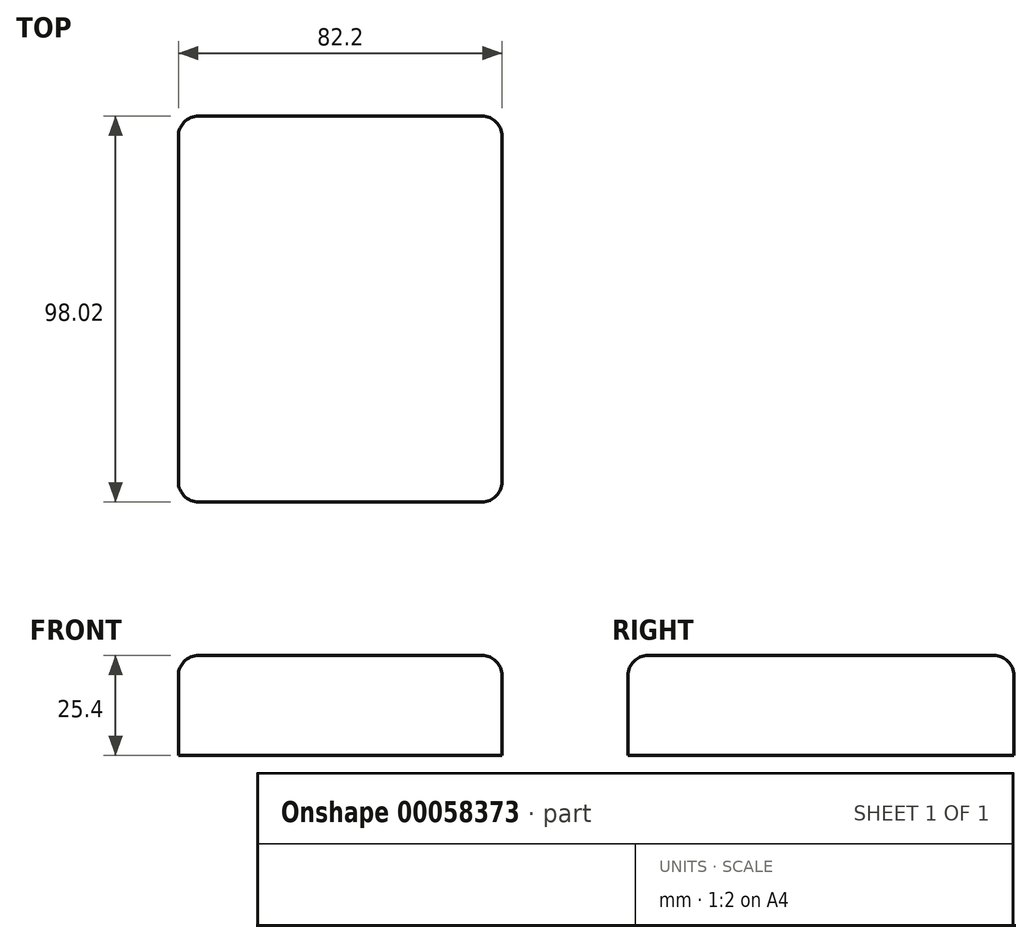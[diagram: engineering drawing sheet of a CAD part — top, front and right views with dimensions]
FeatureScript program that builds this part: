
annotation { "Feature Type Name" : "Feature", "Feature Type Description" : "" }
export const myFeature = defineFeature(function(context is Context, id is Id, definition is map)
    precondition{}
    {
        {
            var Q0;
            Q0=qCreatedBy(makeId("Top.planeOp"),FACE);
            var sketch = newSketch(context, id + "F0", { "sketchPlane" : qUnion([Q0])});
            skLineSegment(sketch, "E0.bottom", {"start": v(-16.47, 59.91) * mm, "end": v(65.73, 59.91) * mm});
            skLineSegment(sketch, "E0.top", {"start": v(-16.47, -38.1) * mm, "end": v(65.73, -38.1) * mm});
            skLineSegment(sketch, "E0.left", {"start": v(-16.47, 59.91) * mm, "end": v(-16.47, -38.1) * mm});
            skLineSegment(sketch, "E0.right", {"start": v(65.73, 59.91) * mm, "end": v(65.73, -38.1) * mm});
            skSolve(sketch);
        }
        {
            var Q0;
            Q0 = qSketchRegion(id + "F0", true);
            extrude(context, id + "F1", {"entities" : qUnion([Q0]), "depth" : 25.4 * mm});
        }
        {
            var Q0;
            Q0=makeQuery(id+"F1.opExtrude","CAP_FACE",FACE,{"disambiguationData":[OSD([sQuery(id+"F0.wireOp",EDGE,"E0.bottom"),sQuery(id+"F0.wireOp",EDGE,"E0.top"),sQuery(id+"F0.wireOp",EDGE,"E0.left"),sQuery(id+"F0.wireOp",EDGE,"E0.right")])],"isStart":false});
            var Q1;
            Q1=makeQuery(id+"F1.opExtrude","SWEPT_EDGE",EDGE,{"disambiguationData":[OSD([sQuery(id+"F0.wireOp",EDGE,"E0.top"),sQuery(id+"F0.wireOp",EDGE,"E0.left")])]});
            var Q2;
            Q2=makeQuery(id+"F1.opExtrude","SWEPT_EDGE",EDGE,{"disambiguationData":[OSD([sQuery(id+"F0.wireOp",EDGE,"E0.top"),sQuery(id+"F0.wireOp",EDGE,"E0.right")])]});
            var Q3;
            Q3=makeQuery(id+"F1.opExtrude","SWEPT_EDGE",EDGE,{"disambiguationData":[OSD([sQuery(id+"F0.wireOp",EDGE,"E0.bottom"),sQuery(id+"F0.wireOp",EDGE,"E0.right")])]});
            var Q4;
            Q4=makeQuery(id+"F1.opExtrude","SWEPT_EDGE",EDGE,{"disambiguationData":[OSD([sQuery(id+"F0.wireOp",EDGE,"E0.bottom"),sQuery(id+"F0.wireOp",EDGE,"E0.left")])]});
            fillet(context, id + "F2", {"entities" : qUnion([Q0, Q1, Q2, Q3, Q4]), "radius" : 5.08 * mm, "tangentPropagation" : true, "allowEdgeOverflow" : false});
        }
    });
